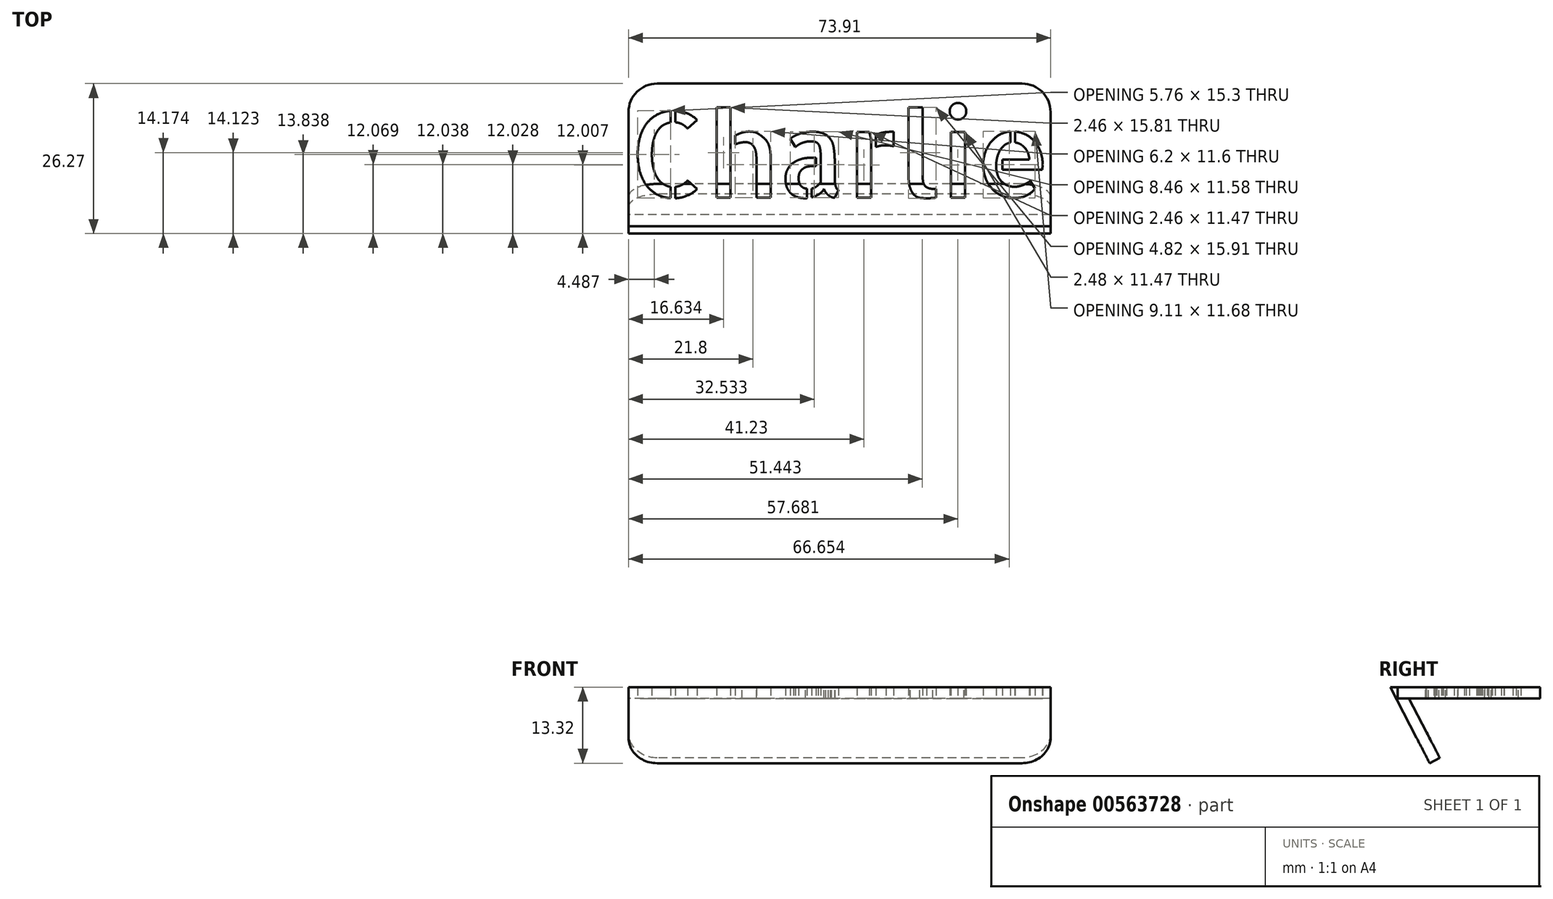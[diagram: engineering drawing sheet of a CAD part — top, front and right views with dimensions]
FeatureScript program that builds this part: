
annotation { "Feature Type Name" : "Feature", "Feature Type Description" : "" }
export const myFeature = defineFeature(function(context is Context, id is Id, definition is map)
    precondition{}
    {
        {
            var Q0;
            Q0=qCreatedBy(makeId("Top.planeOp"),FACE);
            var sketch = newSketch(context, id + "F0", { "sketchPlane" : qUnion([Q0])});
            skLineSegment(sketch, "E0.bottom", {"start": v(-23.58, 12.5) * mm, "end": v(50.33, 12.5) * mm});
            skLineSegment(sketch, "E0.top", {"start": v(-23.58, -12.5) * mm, "end": v(50.33, -12.5) * mm});
            skLineSegment(sketch, "E0.left", {"start": v(-23.58, 12.5) * mm, "end": v(-23.58, -12.5) * mm});
            skLineSegment(sketch, "E0.right", {"start": v(50.33, 12.5) * mm, "end": v(50.33, -12.5) * mm});
            skText(sketch, "E1", { "text": "Charlie", "fontName": "AllertaStencil-Regular.ttf"});
            const initialGuessF0  = {"E1": [-0.02358, -0.0075, 1, 0, 0.015]};
            skSetInitialGuess(sketch, initialGuessF0);
            skSolve(sketch);
        }
        {
            var Q0;
            Q0=makeQuery(id+"F0.imprint","IMPRINT",FACE,{"disambiguationData":[TD([[makeQuery(id+"F0.imprint","IMPRINT",EDGE,{"derivedFrom":sQuery(id+"F0.wireOp",EDGE,"E0.bottom")}),-1.0]])]});
            extrude(context, id + "F1", {"entities" : qUnion([Q0]), "depth" : 2 * mm, "offsetDistance" : 25 * mm});
        }
        {
            var Q0;
            {var subQ0=sQuery(id+"F0.wireOp",EDGE,"E0.left");Q0=makeQuery(id+"FYEOEdhl7jzHk82_2.opBoolean","MERGE",FACE,{"derivedFrom":[makeQuery(id+"F1.opExtrude","SWEPT_FACE",FACE,{"disambiguationData":[OSD([subQ0])]}),makeQuery(id+"FOv1BJgTRWeWuMw_1.opExtrude","CAP_FACE",FACE,{"disambiguationData":[OSD([sQuery(id+"F0.wireOp",EDGE,"E0.bottom"),subQ0,sQuery(id+"Fjco5yBOxZZxTCI_1.wireOp",EDGE,"TpTMtmOo-qoIM-rLEy-p7IH-mKgsBanMGF23"),sQuery(id+"Fjco5yBOxZZxTCI_1.wireOp",EDGE,"Ja6BvVoQ-cpFi-Lcom-cL8s-5xC4kZiynyNl"),sQuery(id+"Fjco5yBOxZZxTCI_1.wireOp",EDGE,"utNyaJ8P-FD6r-AD7x-tpFW-fHytfVhziHLl"),sQuery(id+"Fjco5yBOxZZxTCI_1.wireOp",EDGE,"xGzW29bi-H5H8-ObLh-gdKj-mSPkAtMAUUzO")])],"isStart":true})]});}
            var sketch = newSketch(context, id + "F2", { "sketchPlane" : qUnion([Q0])});
            skLineSegment(sketch, "E2", {"start": v(11.52, 2) * mm, "end": v(5.09, -10.4) * mm});
            skLineSegment(sketch, "E3", {"start": v(5.09, -10.4) * mm, "end": v(6.87, -11.32) * mm});
            skLineSegment(sketch, "E4", {"start": v(6.87, -11.32) * mm, "end": v(13.77, 2) * mm});
            skLineSegment(sketch, "E5", {"start": v(13.77, 2) * mm, "end": v(11.52, 2) * mm});
            skSolve(sketch);
        }
        {
            var Q0;
            {var subQ4=sQuery(id+"F2.wireOp",EDGE,"E3");Q0=makeQuery(id+"F2.imprint","IMPRINT",FACE,{"disambiguationData":[TD([[makeQuery(id+"F2.imprint","IMPRINT",EDGE,{"derivedFrom":subQ4}),1.0]])]});}
            var Q1;
            Q1=makeQuery(id+"F1.opExtrude","SWEPT_FACE",FACE,{"disambiguationData":[OSD([sQuery(id+"F0.wireOp",EDGE,"E0.right")])]});
            extrude(context, id + "F3", {"entities" : qUnion([Q0]), "endBound" : BoundingType.UP_TO_SURFACE, "oppositeDirection" : true, "depth" : 75 * mm, "endBoundEntityFace" : qUnion([Q1]), "offsetDistance" : 25 * mm});
        }
        {
            var Q0;
            Q0=makeQuery(id+"F1.opExtrude","SWEPT_EDGE",EDGE,{"disambiguationData":[OSD([sQuery(id+"F0.wireOp",EDGE,"E0.bottom"),sQuery(id+"F0.wireOp",EDGE,"E0.left")])]});
            var Q1;
            Q1=makeQuery(id+"F1.opExtrude","SWEPT_EDGE",EDGE,{"disambiguationData":[OSD([sQuery(id+"F0.wireOp",EDGE,"E0.bottom"),sQuery(id+"F0.wireOp",EDGE,"E0.right")])]});
            var Q2;
            Q2=makeQuery(id+"F3.opExtrude","CAP_EDGE",EDGE,{"disambiguationData":[OSD([sQuery(id+"F2.wireOp",EDGE,"E3")])],"isStart":false});
            var Q3;
            Q3=makeQuery(id+"F3.opExtrude","CAP_EDGE",EDGE,{"disambiguationData":[OSD([sQuery(id+"F2.wireOp",EDGE,"E3")])],"isStart":true});
            var Q4;
            Q4=makeQuery(id+"F3.opExtrude","TWEAK_EDGE",EDGE,{"derivedFrom":[makeQuery(id+"F1.opExtrude","SWEPT_FACE",FACE,{"disambiguationData":[OSD([sQuery(id+"F0.wireOp",EDGE,"E0.right")])]}),makeQuery(id+"F2.imprint","IMPRINT",EDGE,{"derivedFrom":sQuery(id+"F2.wireOp",EDGE,"E3")})]});
            fillet(context, id + "F4", {"entities" : qUnion([Q0, Q1, Q2, Q3, Q4]), "radius" : 5 * mm, "tangentPropagation" : true, "allowEdgeOverflow" : false});
        }
    });
